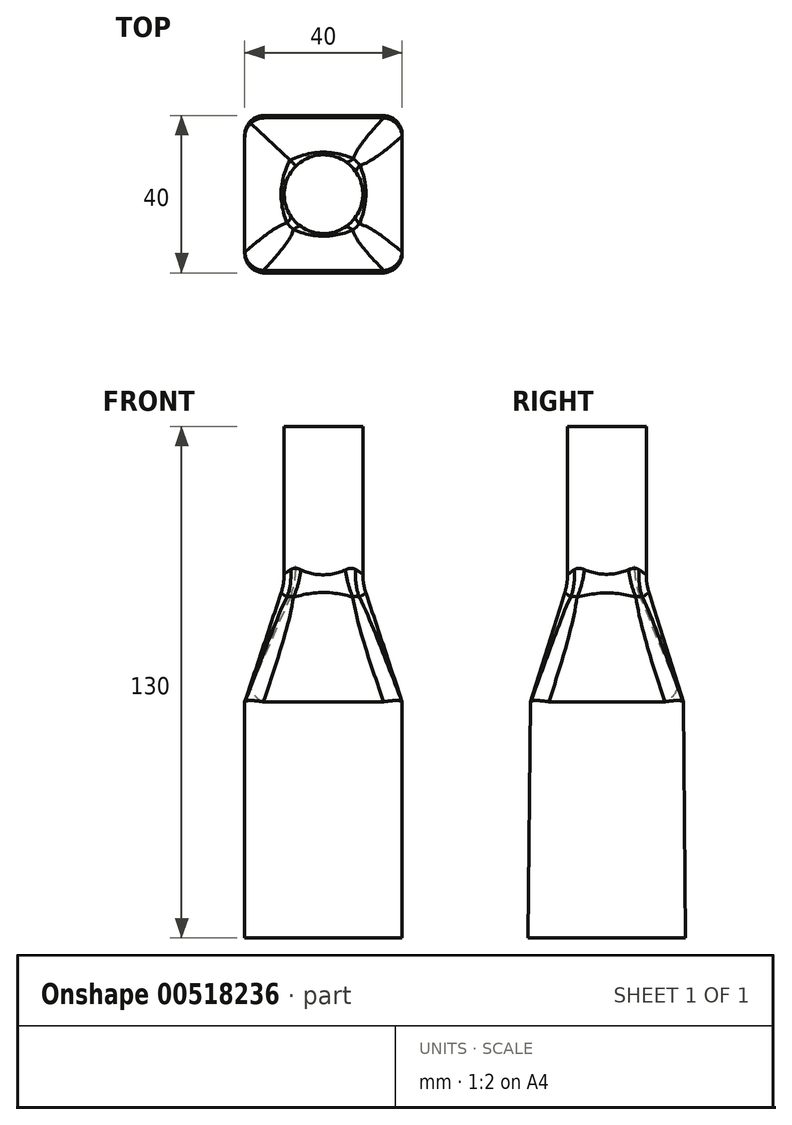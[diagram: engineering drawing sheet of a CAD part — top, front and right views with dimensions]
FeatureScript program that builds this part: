
annotation { "Feature Type Name" : "Feature", "Feature Type Description" : "" }
export const myFeature = defineFeature(function(context is Context, id is Id, definition is map)
    precondition{}
    {
        {
            var Q0;
            Q0=qCreatedBy(makeId("Top.planeOp"),FACE);
            var sketch = newSketch(context, id + "F0", { "sketchPlane" : qUnion([Q0])});
            skLineSegment(sketch, "E0.bottom", {"start": v(20, 20) * mm, "end": v(-20, 20) * mm});
            skLineSegment(sketch, "E0.top", {"start": v(20, -20) * mm, "end": v(-20, -20) * mm});
            skLineSegment(sketch, "E0.left", {"start": v(20, 20) * mm, "end": v(20, -20) * mm});
            skLineSegment(sketch, "E0.right", {"start": v(-20, 20) * mm, "end": v(-20, -20) * mm});
            skPoint(sketch, "E0.middle", {"position": v(0, 0) * mm});
            skSolve(sketch);
        }
        {
            var Q0;
            Q0=qCreatedBy(makeId("Top.planeOp"),FACE);
            cPlane(context, id + "F1", {"entities" : qUnion([Q0]), "cplaneType" : CPlaneType.OFFSET, "offset" : 60 * mm, "width" : 150 * mm, "height" : 150 * mm});
        }
        {
            var Q0;
            Q0=qCreatedBy(id+"F1.planeOp",FACE);
            var sketch = newSketch(context, id + "F2", { "sketchPlane" : qUnion([Q0])});
            skLineSegment(sketch, "E1.bottom", {"start": v(20, 19.4) * mm, "end": v(-20, 19.4) * mm});
            skLineSegment(sketch, "E1.top", {"start": v(20, -19.4) * mm, "end": v(-20, -19.4) * mm});
            skLineSegment(sketch, "E1.left", {"start": v(20, 19.4) * mm, "end": v(20, -19.4) * mm});
            skLineSegment(sketch, "E1.right", {"start": v(-20, 19.4) * mm, "end": v(-20, -19.4) * mm});
            skPoint(sketch, "E1.middle", {"position": v(0, 0) * mm});
            skSolve(sketch);
        }
        {
            var Q0;
            Q0=qCreatedBy(id+"F1.planeOp",FACE);
            cPlane(context, id + "F3", {"entities" : qUnion([Q0]), "cplaneType" : CPlaneType.OFFSET, "offset" : 30 * mm, "width" : 150 * mm, "height" : 150 * mm});
        }
        {
            var Q0;
            Q0=qCreatedBy(id+"F3.planeOp",FACE);
            var sketch = newSketch(context, id + "F4", { "sketchPlane" : qUnion([Q0])});
            skCircle(sketch, "E2", {"center": v(0, 0) * mm, "radius": 10 * mm});
            skSolve(sketch);
        }
        {
            var Q0;
            Q0=qCreatedBy(id+"F3.planeOp",FACE);
            cPlane(context, id + "F5", {"entities" : qUnion([Q0]), "cplaneType" : CPlaneType.OFFSET, "offset" : 40 * mm, "width" : 150 * mm, "height" : 150 * mm});
        }
        {
            var Q0;
            Q0=qCreatedBy(id+"F5.planeOp",FACE);
            var sketch = newSketch(context, id + "F6", { "sketchPlane" : qUnion([Q0])});
            skCircle(sketch, "E3", {"center": v(0, 0) * mm, "radius": 10 * mm});
            skSolve(sketch);
        }
        {
            var Q0;
            Q0=makeQuery(id+"F0.imprint","IMPRINT",FACE,{"disambiguationData":[TD([[makeQuery(id+"F0.imprint","IMPRINT",EDGE,{"derivedFrom":sQuery(id+"F0.wireOp",EDGE,"E0.bottom")}),1.0]])]});
            var Q1;
            Q1=makeQuery(id+"F2.imprint","IMPRINT",FACE,{"disambiguationData":[TD([[makeQuery(id+"F2.imprint","IMPRINT",EDGE,{"derivedFrom":sQuery(id+"F2.wireOp",EDGE,"E1.bottom")}),1.0]])]});
            loft(context, id + "F7", {"sheetProfilesArray" : [{ "sheetProfileEntities" : qUnion([Q0]) }, { "sheetProfileEntities" : qUnion([Q1]) }]});
        }
        {
            var Q1;
            Q1=makeQuery(id+"F7.opLoft","CAP_FACE",FACE,{"disambiguationData":[OSD([makeQuery(id+"F2.imprint","IMPRINT",FACE,{"disambiguationData":[TD([[makeQuery(id+"F2.imprint","IMPRINT",EDGE,{"derivedFrom":sQuery(id+"F2.wireOp",EDGE,"E1.bottom")}),1.0]])]})])],"isStart":true});
            var Q2;
            Q2=makeQuery(id+"F4.imprint","IMPRINT",FACE,{"disambiguationData":[TD([[makeQuery(id+"F4.imprint","IMPRINT",EDGE,{"derivedFrom":sQuery(id+"F4.wireOp",EDGE,"E2")}),1.0]])]});
            loft(context, id + "F8", {"operationType" : NewBodyOperationType.ADD, "sheetProfilesArray" : [{ "sheetProfileEntities" : qUnion([Q1]) }, { "sheetProfileEntities" : qUnion([Q2]) }]});
        }
        {
            var Q1;
            Q1=makeQuery(id+"F6.imprint","IMPRINT",FACE,{"disambiguationData":[TD([[makeQuery(id+"F6.imprint","IMPRINT",EDGE,{"derivedFrom":sQuery(id+"F6.wireOp",EDGE,"E3")}),1.0]])]});
            var Q2;
            Q2=makeQuery(id+"F8.opLoft","CAP_FACE",FACE,{"disambiguationData":[OSD([makeQuery(id+"F4.imprint","IMPRINT",FACE,{"disambiguationData":[TD([[makeQuery(id+"F4.imprint","IMPRINT",EDGE,{"derivedFrom":sQuery(id+"F4.wireOp",EDGE,"E2")}),1.0]])]})])],"isStart":true});
            loft(context, id + "F9", {"operationType" : NewBodyOperationType.ADD, "sheetProfilesArray" : [{ "sheetProfileEntities" : qUnion([Q1]) }, { "sheetProfileEntities" : qUnion([Q2]) }]});
        }
        {
            var Q0;
            Q0=makeQuery(id+"F7.opLoft","SWEPT_EDGE",EDGE,{"disambiguationData":[OSD([sQuery(id+"F0.wireOp",EDGE,"E0.bottom"),sQuery(id+"F0.wireOp",EDGE,"E0.right"),sQuery(id+"F2.wireOp",EDGE,"E1.bottom"),sQuery(id+"F2.wireOp",EDGE,"E1.right")])]});
            var Q1;
            Q1=makeQuery(id+"F7.opLoft","SWEPT_EDGE",EDGE,{"disambiguationData":[OSD([sQuery(id+"F0.wireOp",EDGE,"E0.bottom"),sQuery(id+"F0.wireOp",EDGE,"E0.left"),sQuery(id+"F2.wireOp",EDGE,"E1.bottom"),sQuery(id+"F2.wireOp",EDGE,"E1.left")])]});
            var Q2;
            Q2=makeQuery(id+"F7.opLoft","SWEPT_EDGE",EDGE,{"disambiguationData":[OSD([sQuery(id+"F0.wireOp",EDGE,"E0.top"),sQuery(id+"F0.wireOp",EDGE,"E0.right"),sQuery(id+"F2.wireOp",EDGE,"E1.top"),sQuery(id+"F2.wireOp",EDGE,"E1.right")])]});
            var Q3;
            Q3=makeQuery(id+"F7.opLoft","SWEPT_EDGE",EDGE,{"disambiguationData":[OSD([sQuery(id+"F0.wireOp",EDGE,"E0.top"),sQuery(id+"F0.wireOp",EDGE,"E0.left"),sQuery(id+"F2.wireOp",EDGE,"E1.top"),sQuery(id+"F2.wireOp",EDGE,"E1.left")])]});
            var Q4;
            Q4=makeQuery(id+"F8.opLoft","SWEPT_EDGE",EDGE,{"disambiguationData":[OSD([sQuery(id+"F2.wireOp",EDGE,"E1.bottom"),sQuery(id+"F2.wireOp",EDGE,"E1.top"),sQuery(id+"F2.wireOp",EDGE,"E1.right"),sQuery(id+"F4.wireOp",EDGE,"E2")])]});
            var Q5;
            Q5=makeQuery(id+"F8.opLoft","SWEPT_EDGE",EDGE,{"disambiguationData":[OSD([sQuery(id+"F2.wireOp",EDGE,"E1.bottom"),sQuery(id+"F2.wireOp",EDGE,"E1.left"),sQuery(id+"F2.wireOp",EDGE,"E1.right"),sQuery(id+"F4.wireOp",EDGE,"E2")])]});
            var Q6;
            Q6=makeQuery(id+"F8.opLoft","SWEPT_EDGE",EDGE,{"disambiguationData":[OSD([sQuery(id+"F2.wireOp",EDGE,"E1.bottom"),sQuery(id+"F2.wireOp",EDGE,"E1.left")])]});
            var Q7;
            Q7=makeQuery(id+"F8.opLoft","SWEPT_EDGE",EDGE,{"disambiguationData":[OSD([sQuery(id+"F2.wireOp",EDGE,"E1.top"),sQuery(id+"F2.wireOp",EDGE,"E1.left"),sQuery(id+"F2.wireOp",EDGE,"E1.right"),sQuery(id+"F4.wireOp",EDGE,"E2")])]});
            fillet(context, id + "F10", {"entities" : qUnion([Q0, Q1, Q2, Q3, Q4, Q5, Q6, Q7]), "radius" : 5 * mm, "tangentPropagation" : true, "allowEdgeOverflow" : false});
        }
        {
            var Q0;
            {var subQ0=sQuery(id+"F4.wireOp",EDGE,"E2");var subQ1=sQuery(id+"F2.wireOp",EDGE,"E1.right");var subQ2=sQuery(id+"F2.wireOp",EDGE,"E1.left");var subQ3=sQuery(id+"F2.wireOp",EDGE,"E1.bottom");Q0=makeQuery(id+"F9.boolean.opBoolean","MERGE",EDGE,{"derivedFrom":[makeQuery(id+"F8.opLoft","MID_CAP_EDGE",EDGE,{"disambiguationData":[OSD([subQ3,subQ2,subQ1,subQ0])],"capPos":1.0}),makeQuery(id+"F9.opLoft","MID_CAP_EDGE",EDGE,{"disambiguationData":[OSD([subQ3,subQ2,subQ1,subQ0])],"capPos":1.0})]});}
            var Q1;
            {var subQ0=sQuery(id+"F4.wireOp",EDGE,"E2");var subQ1=sQuery(id+"F2.wireOp",EDGE,"E1.right");var subQ2=sQuery(id+"F2.wireOp",EDGE,"E1.top");var subQ3=sQuery(id+"F2.wireOp",EDGE,"E1.bottom");Q1=makeQuery(id+"F9.boolean.opBoolean","MERGE",EDGE,{"derivedFrom":[makeQuery(id+"F8.opLoft","MID_CAP_EDGE",EDGE,{"disambiguationData":[OSD([subQ3,subQ2,subQ1,subQ0])],"capPos":1.0}),makeQuery(id+"F9.opLoft","MID_CAP_EDGE",EDGE,{"disambiguationData":[OSD([subQ3,subQ2,subQ1,subQ0])],"capPos":1.0})]});}
            var Q2;
            {var subQ0=sQuery(id+"F4.wireOp",EDGE,"E2");var subQ1=sQuery(id+"F2.wireOp",EDGE,"E1.left");var subQ2=sQuery(id+"F2.wireOp",EDGE,"E1.bottom");Q2=makeQuery(id+"F9.boolean.opBoolean","MERGE",EDGE,{"derivedFrom":[makeQuery(id+"F8.opLoft","MID_CAP_EDGE",EDGE,{"disambiguationData":[OSD([subQ2,subQ1,subQ0])],"capPos":1.0}),makeQuery(id+"F9.opLoft","MID_CAP_EDGE",EDGE,{"disambiguationData":[OSD([subQ2,subQ1,subQ0])],"capPos":1.0})]});}
            var Q3;
            {var subQ0=sQuery(id+"F4.wireOp",EDGE,"E2");var subQ1=sQuery(id+"F2.wireOp",EDGE,"E1.right");var subQ2=sQuery(id+"F2.wireOp",EDGE,"E1.left");var subQ3=sQuery(id+"F2.wireOp",EDGE,"E1.top");var subQ4=sQuery(id+"F2.wireOp",EDGE,"E1.bottom");Q3=makeQuery(id+"F9.boolean.opBoolean","MERGE",EDGE,{"derivedFrom":[makeQuery(id+"F8.opLoft","MID_CAP_EDGE",EDGE,{"disambiguationData":[OSD([subQ4,subQ3,subQ2,subQ1,subQ0])],"capPos":1.0}),makeQuery(id+"F9.opLoft","MID_CAP_EDGE",EDGE,{"disambiguationData":[OSD([subQ4,subQ3,subQ2,subQ1,subQ0])],"capPos":1.0})]});}
            fillet(context, id + "F11", {"entities" : qUnion([Q0, Q1, Q2, Q3]), "radius" : 15 * mm, "tangentPropagation" : true, "allowEdgeOverflow" : false});
        }
    });
